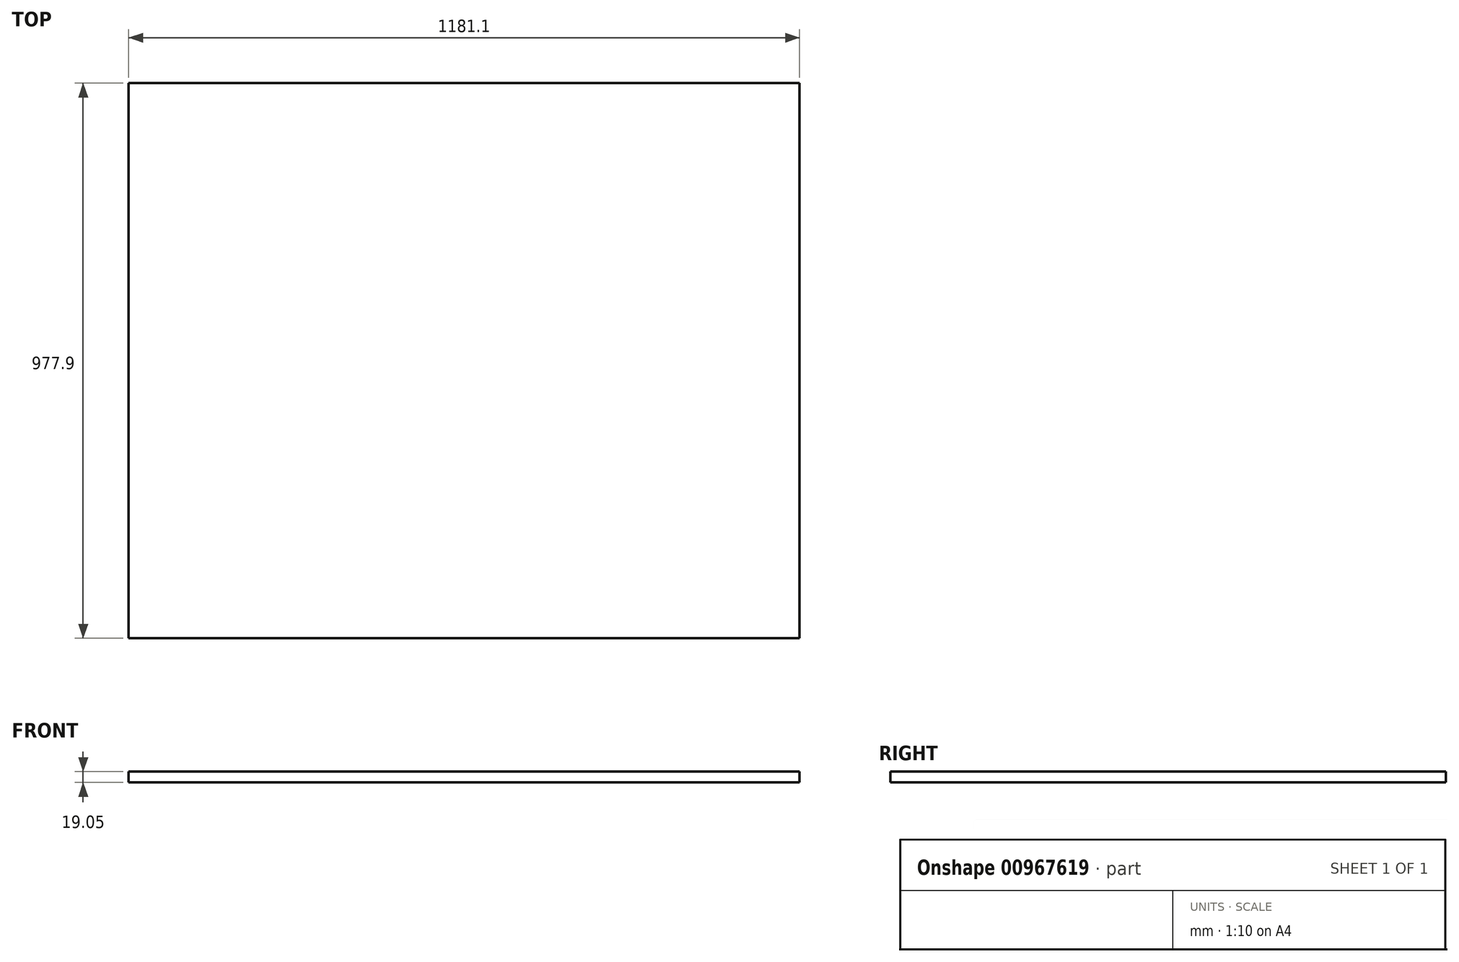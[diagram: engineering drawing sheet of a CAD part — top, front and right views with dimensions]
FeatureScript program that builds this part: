
annotation { "Feature Type Name" : "Feature", "Feature Type Description" : "" }
export const myFeature = defineFeature(function(context is Context, id is Id, definition is map)
    precondition{}
    {
        {
            var Q0;
            Q0=qCreatedBy(makeId("Top.planeOp"),FACE);
            var sketch = newSketch(context, id + "F0", { "sketchPlane" : qUnion([Q0])});
            skLineSegment(sketch, "E0.bottom", {"start": v(590.55, 488.95) * mm, "end": v(-590.55, 488.95) * mm});
            skLineSegment(sketch, "E0.top", {"start": v(590.55, -488.95) * mm, "end": v(-590.55, -488.95) * mm});
            skLineSegment(sketch, "E0.left", {"start": v(590.55, 488.95) * mm, "end": v(590.55, -488.95) * mm});
            skLineSegment(sketch, "E0.right", {"start": v(-590.55, 488.95) * mm, "end": v(-590.55, -488.95) * mm});
            skPoint(sketch, "E0.middle", {"position": v(0, 0) * mm});
            skSolve(sketch);
        }
        {
            var Q0;
            Q0=makeQuery(id+"F0.imprint","IMPRINT",FACE,{"disambiguationData":[TD([[makeQuery(id+"F0.imprint","IMPRINT",EDGE,{"derivedFrom":sQuery(id+"F0.wireOp",EDGE,"E0.bottom")}),1.0]])]});
            extrude(context, id + "F1", {"entities" : qUnion([Q0]), "depth" : 19.05 * mm, "offsetDistance" : 25.4 * mm});
        }
    });
